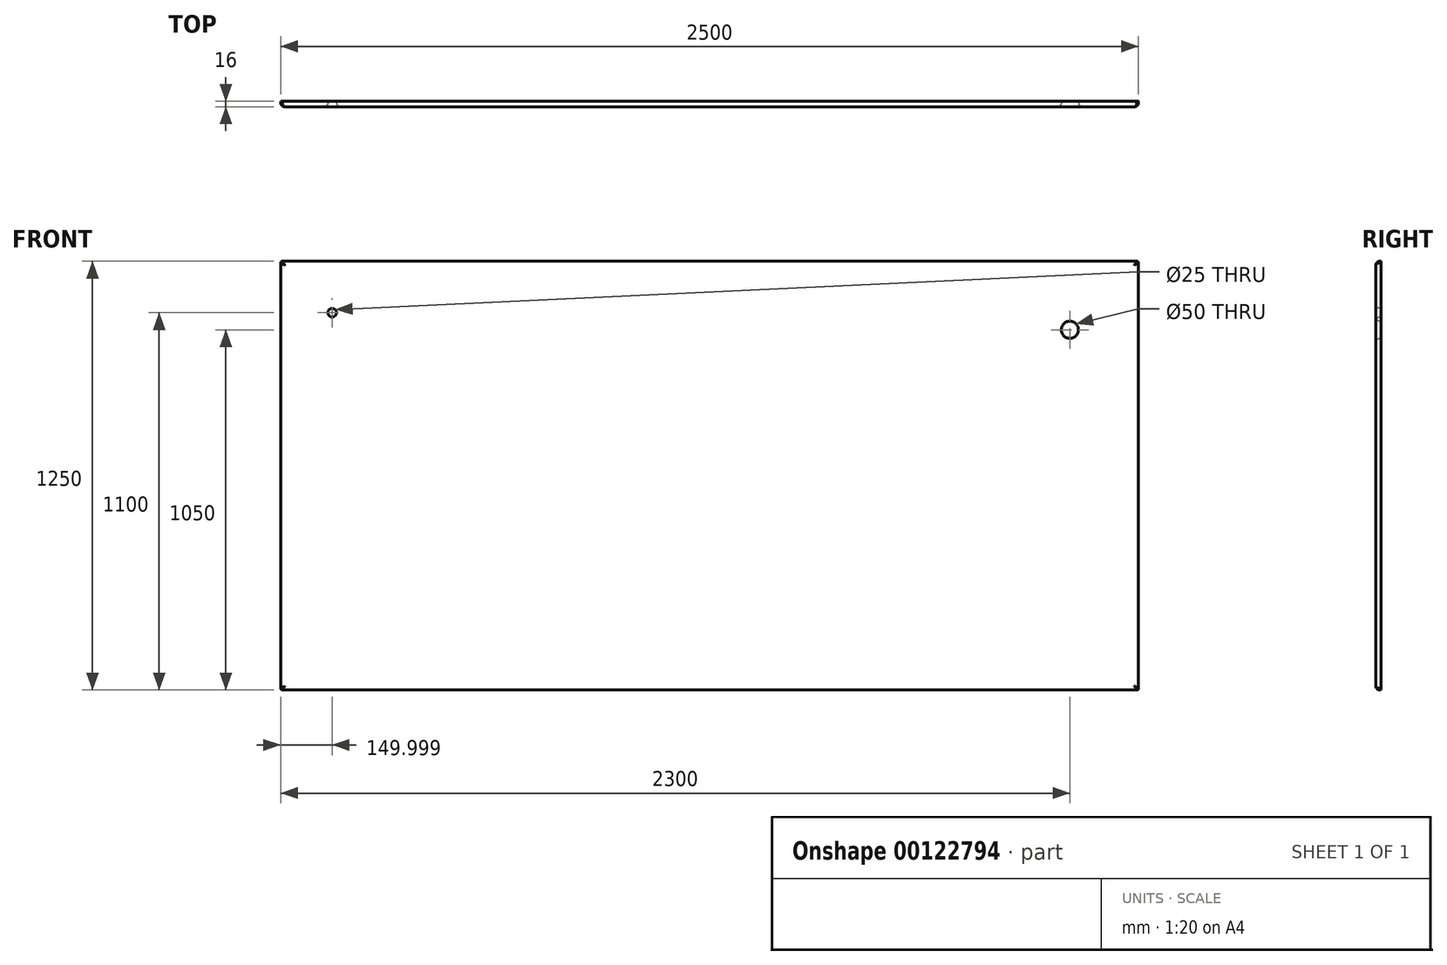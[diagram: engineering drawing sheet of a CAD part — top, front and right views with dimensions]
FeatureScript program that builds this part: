
annotation { "Feature Type Name" : "Feature", "Feature Type Description" : "" }
export const myFeature = defineFeature(function(context is Context, id is Id, definition is map)
    precondition{}
    {
        {
            var Q0;
            Q0=qCreatedBy(makeId("Front.planeOp"),FACE);
            var sketch = newSketch(context, id + "F0", { "sketchPlane" : qUnion([Q0])});
            skLineSegment(sketch, "E0.bottom", {"start": v(1233.49, 665.43) * mm, "end": v(-1256.51, 665.43) * mm});
            skLineSegment(sketch, "E0.top", {"start": v(1233.49, -584.57) * mm, "end": v(-1256.51, -584.57) * mm});
            skLineSegment(sketch, "E0.left", {"start": v(1238.49, 660.43) * mm, "end": v(1238.49, -579.57) * mm});
            skLineSegment(sketch, "E0.right", {"start": v(-1261.51, 660.43) * mm, "end": v(-1261.51, -579.57) * mm});
            skPoint(sketch, "E1.visualSharp", {"position": v(-1261.51, 665.43) * mm});
            skArc(sketch, "E1.filletArc", {"start": v(-1256.51, 665.43) * mm, "mid": v(-1260.05, 663.96) * mm, "end": v(-1261.51, 660.43) * mm});
            skPoint(sketch, "E2.visualSharp", {"position": v(1238.49, 665.43) * mm});
            skArc(sketch, "E2.filletArc", {"start": v(1238.49, 660.43) * mm, "mid": v(1237.02, 663.96) * mm, "end": v(1233.49, 665.43) * mm});
            skPoint(sketch, "E3.visualSharp", {"position": v(-1261.51, -584.57) * mm});
            skArc(sketch, "E3.filletArc", {"start": v(-1261.51, -579.57) * mm, "mid": v(-1260.05, -583.1) * mm, "end": v(-1256.51, -584.57) * mm});
            skPoint(sketch, "E4.visualSharp", {"position": v(1238.49, -584.57) * mm});
            skArc(sketch, "E4.filletArc", {"start": v(1233.49, -584.57) * mm, "mid": v(1237.02, -583.1) * mm, "end": v(1238.49, -579.57) * mm});
            skCircle(sketch, "E5", {"center": v(-1111.51, 515.43) * mm, "radius": 12.5 * mm});
            skCircle(sketch, "E6", {"center": v(1038.49, 465.43) * mm, "radius": 25 * mm});
            skSolve(sketch);
        }
        {
            var Q0;
            Q0=makeQuery(id+"F0.imprint","IMPRINT",FACE,{"disambiguationData":[TD([[makeQuery(id+"F0.imprint","IMPRINT",EDGE,{"derivedFrom":sQuery(id+"F0.wireOp",EDGE,"E0.bottom")}),1.0]])]});
            extrude(context, id + "F1", {"entities" : qUnion([Q0]), "depth" : 16 * mm});
        }
        {
            var Q0;
            Q0=makeQuery(id+"F1.opExtrude","CAP_FACE",FACE,{"disambiguationData":[OSD([sQuery(id+"F0.wireOp",EDGE,"E0.bottom"),sQuery(id+"F0.wireOp",EDGE,"E0.top"),sQuery(id+"F0.wireOp",EDGE,"E0.left"),sQuery(id+"F0.wireOp",EDGE,"E0.right")])],"isStart":false});
            var Q1;
            Q1=makeQuery(id+"F1.opExtrude","CAP_EDGE",EDGE,{"disambiguationData":[OSD([sQuery(id+"F0.wireOp",EDGE,"E0.right")])],"isStart":false});
            var Q2;
            Q2=makeQuery(id+"F1.opExtrude","CAP_EDGE",EDGE,{"disambiguationData":[OSD([sQuery(id+"F0.wireOp",EDGE,"E0.top")])],"isStart":false});
            var Q3;
            Q3=makeQuery(id+"F1.opExtrude","CAP_EDGE",EDGE,{"disambiguationData":[OSD([sQuery(id+"F0.wireOp",EDGE,"E0.left")])],"isStart":false});
            var Q4;
            Q4=makeQuery(id+"F1.opExtrude","CAP_EDGE",EDGE,{"disambiguationData":[OSD([sQuery(id+"F0.wireOp",EDGE,"E0.bottom")])],"isStart":false});
            fillet(context, id + "F2", {"entities" : qUnion([Q0, Q1, Q2, Q3, Q4]), "radius" : 12 * mm, "tangentPropagation" : true, "allowEdgeOverflow" : false});
        }
    });
